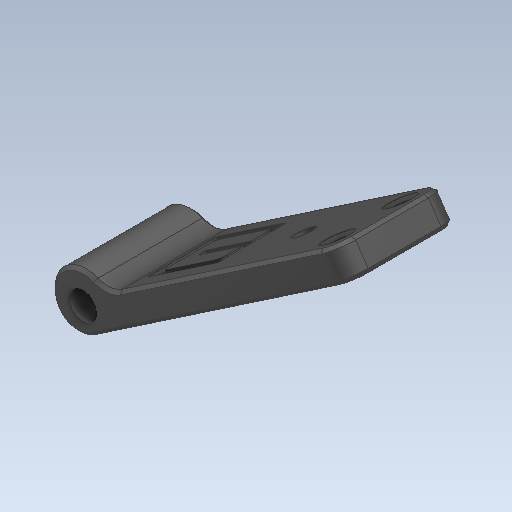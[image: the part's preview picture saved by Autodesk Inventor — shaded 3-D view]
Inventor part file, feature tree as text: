
AUTODESK INVENTOR PART (.ipt)
format: ipt  version: 2020 (Build 240168000, 168)  size: 208,384 bytes
history: native  units: mm
features: extrude x1, sketch x1
ambient origin geometry x8: Origin, YZ Plane, XZ Plane, XY Plane, X Axis, Y Axis, Z Axis, Center Point
bodies: Volumenkörper1 (feature_tree), Body1 (feature_tree)
feature tree (2):
  extrude  "Extrusion1"  Depth=10.0mm TaperAngle=0.0deg
  sketch  "Skizze1"  dims[d0=12.0mm d1=10.0mm d2=0.0mm]
